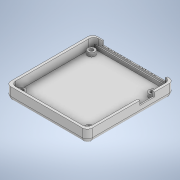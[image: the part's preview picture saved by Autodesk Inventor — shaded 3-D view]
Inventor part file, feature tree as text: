
AUTODESK INVENTOR PART (.ipt)
format: ipt  version: 2021 (Build 250183000, 183)  size: 789,504 bytes
history: native  units: mm
features: extrude x15, sketch x14, projected_geometry x3, fillet x1
ambient origin geometry x8: Origin, YZ Plane, XZ Plane, XY Plane, X Axis, Y Axis, Z Axis, Center Point
bodies: Solid1 (feature_tree)
feature tree (33):
  extrude  "Extrusion1"  Depth=62.0mm
  extrude  "Extrusion2"  Depth=3.0mm
  extrude  "Extrusion56"  Depth=3.0mm
  extrude  "Extrusion58"  Depth=4.5mm
  extrude  "Extrusion59"  Depth=3.0mm
  extrude  "Extrusion60"  Depth=54.35mm
  extrude  "Extrusion61"  Depth=51.56mm
  extrude  "Extrusion62"  Depth=6.0mm
  extrude  "Extrusion63"  Depth=6.0mm
  extrude  "Extrusion64"  Depth=20.0mm
  extrude  "Extrusion65"  Depth=1.0mm
  extrude  "Extrusion66"  Depth=2.5mm
  extrude  "Extrusion67"  Depth=2.5mm
  fillet  "Fillet13"  Radius=2.5mm
  extrude  "Extrusion68"  Depth=2.5mm
  extrude  "Extrusion69"  Depth=3.0mm TaperAngle=0.0deg
  sketch  "Sketch2"  dims[d14=66.0mm d15=62.0mm]
  sketch  "Sketch69"  dims[d16=3.0mm d17=3.0mm]
  sketch  "Sketch72"  dims[d18=3.0mm d19=3.0mm]
  sketch  "Sketch73"  dims[d20=3.0mm d21=4.5mm]
  sketch  "Sketch74"  dims[d22=6.0mm d23=3.0mm]
  sketch  "Sketch75"  dims[d24=57.4mm d25=54.35mm]
  sketch  "Sketch77"  dims[d26=0.8mm d27=51.56mm]
  sketch  "Sketch78"  dims[d28=4.8mm d29=6.0mm]
  projected_geometry  "Projected Loop3"
  projected_geometry  "Projected Loop4"
  sketch  "Sketch80"  dims[d30=6.0mm d31=6.0mm]
  sketch  "Sketch81"  dims[d32=20.0mm d33=20.0mm]
  sketch  "Sketch82"  dims[d34=1.0mm d35=1.0mm]
  projected_geometry  "Projected Loop5"
  sketch  "Sketch83"  dims[d36=2.0mm d37=0.0mm]
  sketch  "Sketch84"  dims[d38=66.0mm d40=3.0mm d41=3.0mm d42=3.0mm d43=3.0mm d44=3.0mm d45=4.5mm d46=6.0mm d47=3.0mm d48=57.4mm d50=0.8mm d51=51.56mm d52=4.8mm d53=6.0mm d54=6.0mm d55=6.0mm d62=3.0mm d63=0.0mm]
  sketch  "Sketch86"  dims[d181=2.0mm d182=2.0mm d184=2.0mm d186=2.0mm d187=8.0mm d190=8.0mm d193=8.0mm d196=8.0mm d432=2.5mm d433=2.5mm d434=2.5mm d435=2.5mm d436=3.0mm d437=0.0mm d446=6.0mm d447=0.0mm d448=6.0mm d449=7.0mm d450=7.1mm d451=2.0mm d452=0.0mm d453=2.0mm d454=6.0mm d455=0.0mm d457=52.5mm d458=1.0mm d459=4.3mm d460=12.0mm d461=3.0mm d462=0.0mm d463=3.0mm d464=0.0mm d465=0.0mm d466=1.5mm d467=0.0mm d469=1.0mm d470=1.5mm d471=0.0mm d472=2.0mm d473=0.0mm d475=4.0mm d476=10.0mm d477=0.0mm d478=4.0mm d479=10.0mm d480=0.0mm d482=1.0mm d483=0.0mm d484=3.0mm d486=3.0mm d487=3.0mm d488=3.0mm d489=1011.0mm d490=0.0mm d491=4.0mm d492=6.0mm d493=6.0mm d494=6.0mm d495=6.0mm d496=2.5mm d497=0.0mm d506=0.0mm d507=2.1mm d508=200.0mm d510=2.54mm d511=10.0mm d513=10.0mm d515=2.0mm d516=2.0mm d517=2.0mm d518=2.0mm d519=0.25mm d520=0.25mm d521=0.25mm d522=0.25mm d523=0.1mm d524=0.5mm d525=0.0mm d528=0.25mm d529=0.25mm d530=0.25mm d531=0.25mm d532=0.25mm d533=0.25mm d534=0.25mm d535=0.25mm d536=0.25mm d537=0.25mm d538=0.25mm d539=0.25mm d540=0.1mm d541=0.1mm d542=0.1mm d543=0.25mm d544=0.25mm d545=0.25mm d546=0.25mm d547=0.25mm d548=0.25mm d549=0.25mm d550=0.25mm d551=0.25mm d552=0.25mm d553=0.25mm d554=0.25mm d555=0.1mm d556=0.1mm d558=0.1mm d409=0.5mm d410=0.872665mm d411=0.5mm d412=0.872665mm d417=0.5mm d418=0.872665mm d419=0.5mm d420=0.872665mm]
